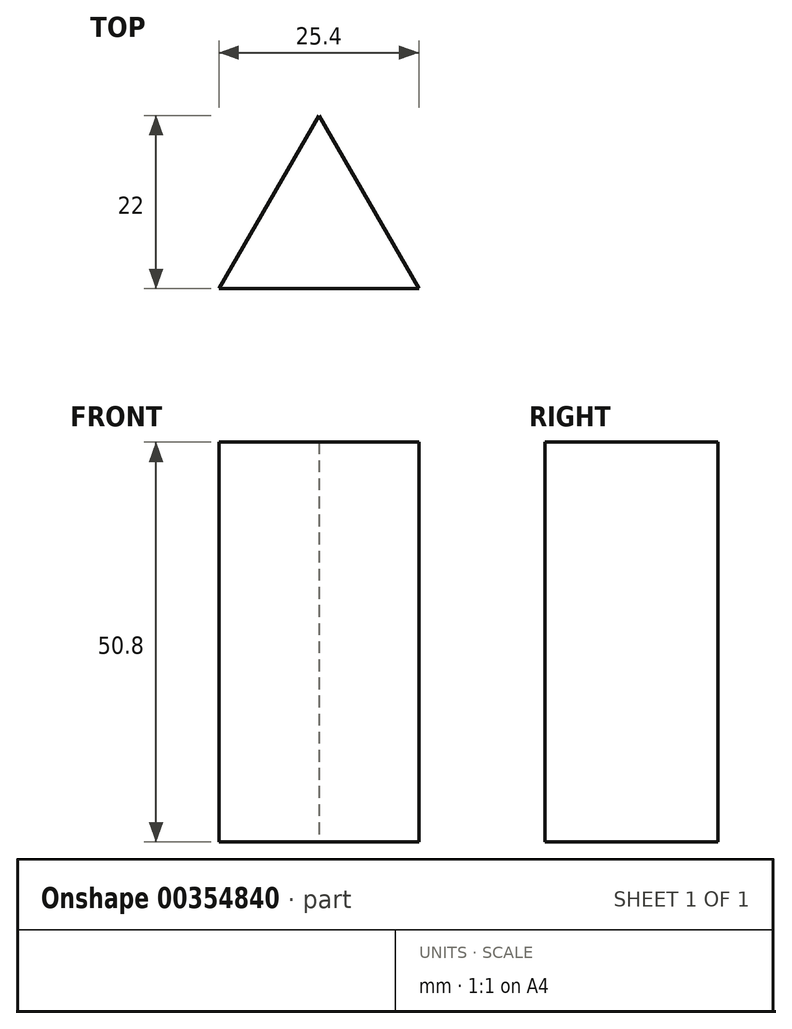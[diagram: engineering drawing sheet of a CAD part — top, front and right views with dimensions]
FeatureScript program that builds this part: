
annotation { "Feature Type Name" : "Feature", "Feature Type Description" : "" }
export const myFeature = defineFeature(function(context is Context, id is Id, definition is map)
    precondition{}
    {
        {
            var Q0;
            Q0=qCreatedBy(makeId("Top.planeOp"),FACE);
            var sketch = newSketch(context, id + "F0", { "sketchPlane" : qUnion([Q0])});
            skLineSegment(sketch, "E0", {"start": v(-12.7, 0) * mm, "end": v(12.7, 0) * mm});
            skLineSegment(sketch, "E1", {"start": v(0, 22) * mm, "end": v(12.7, 0) * mm});
            skLineSegment(sketch, "E2", {"start": v(0, 22) * mm, "end": v(-12.7, 0) * mm});
            skSolve(sketch);
        }
        {
            var Q0;
            Q0=makeQuery(id+"F0.imprint","IMPRINT",FACE,{"disambiguationData":[TD([[makeQuery(id+"F0.imprint","IMPRINT",EDGE,{"derivedFrom":sQuery(id+"F0.wireOp",EDGE,"E0")}),1.0]])]});
            extrude(context, id + "F1", {"entities" : qUnion([Q0]), "depth" : 50.8 * mm});
        }
    });
